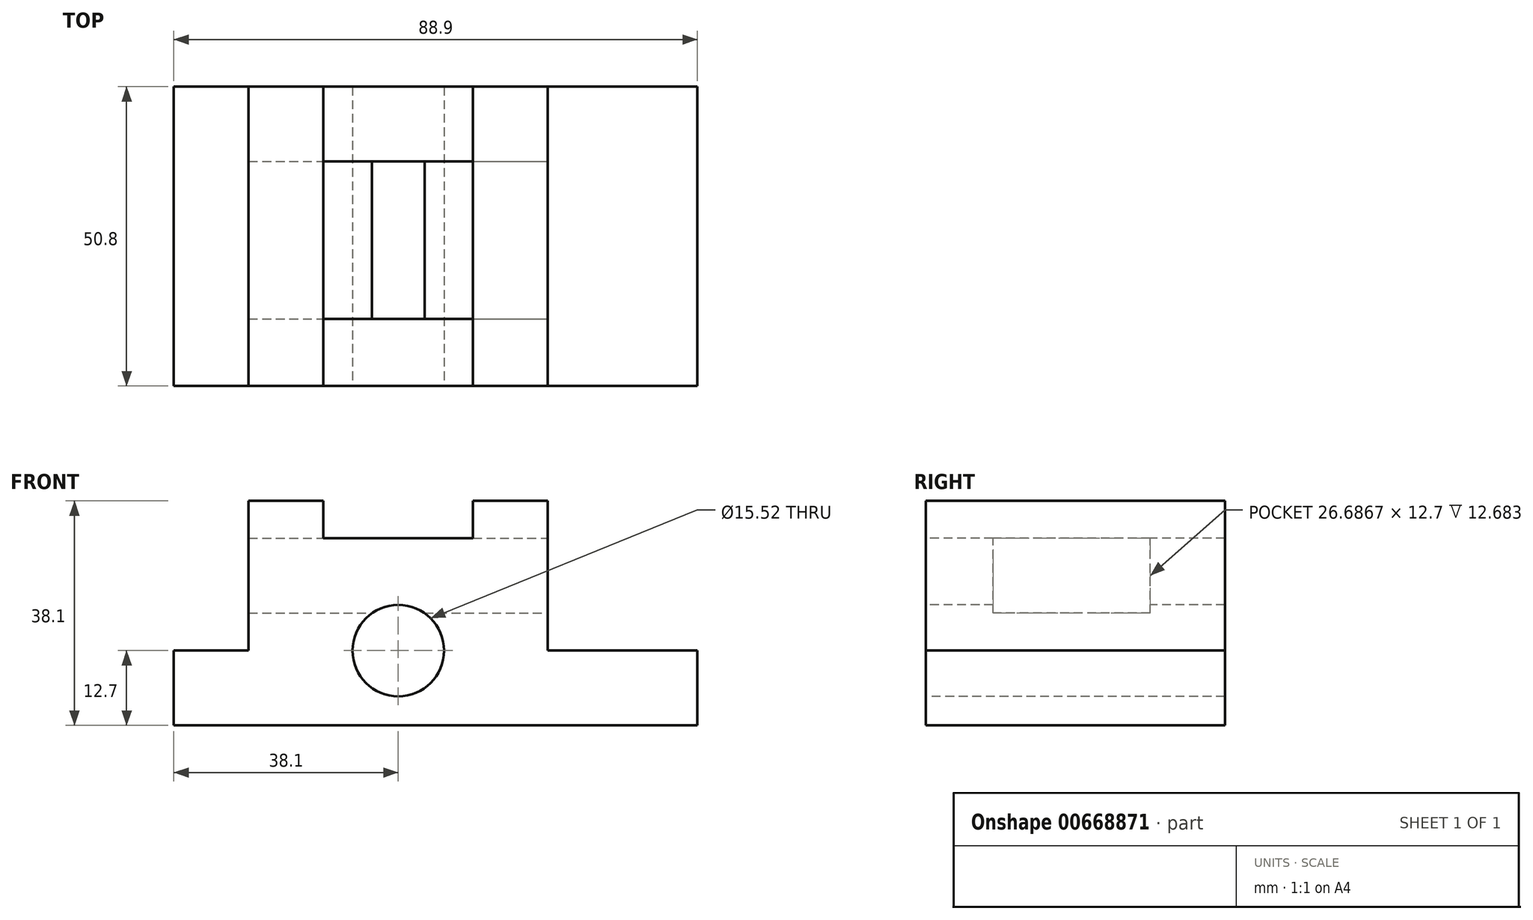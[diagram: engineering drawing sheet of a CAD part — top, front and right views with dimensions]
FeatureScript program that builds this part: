
annotation { "Feature Type Name" : "Feature", "Feature Type Description" : "" }
export const myFeature = defineFeature(function(context is Context, id is Id, definition is map)
    precondition{}
    {
        {
            var Q0;
            Q0=qCreatedBy(makeId("Front.planeOp"),FACE);
            var sketch = newSketch(context, id + "F0", { "sketchPlane" : qUnion([Q0])});
            skLineSegment(sketch, "E0.bottom", {"start": v(44.45, -19.05) * mm, "end": v(-44.45, -19.05) * mm});
            skLineSegment(sketch, "E0.top", {"start": v(44.45, 19.05) * mm, "end": v(-44.45, 19.05) * mm});
            skLineSegment(sketch, "E0.left", {"start": v(44.45, -19.05) * mm, "end": v(44.45, 19.05) * mm});
            skLineSegment(sketch, "E0.right", {"start": v(-44.45, -19.05) * mm, "end": v(-44.45, 19.05) * mm});
            skPoint(sketch, "E0.middle", {"position": v(0, 0) * mm});
            skSolve(sketch);
        }
        {
            var Q0;
            Q0=makeQuery(id+"F0.imprint","IMPRINT",FACE,{"disambiguationData":[TD([[makeQuery(id+"F0.imprint","IMPRINT",EDGE,{"derivedFrom":sQuery(id+"F0.wireOp",EDGE,"E0.bottom")}),-1.0]])]});
            extrude(context, id + "F1", {"entities" : qUnion([Q0]), "depth" : 50.8 * mm, "offsetDistance" : 25.4 * mm});
        }
        {
            var Q0;
            Q0=makeQuery(id+"F1.opExtrude","CAP_FACE",FACE,{"disambiguationData":[OSD([sQuery(id+"F0.wireOp",EDGE,"E0.bottom"),sQuery(id+"F0.wireOp",EDGE,"E0.top"),sQuery(id+"F0.wireOp",EDGE,"E0.left"),sQuery(id+"F0.wireOp",EDGE,"E0.right")])],"isStart":false});
            var sketch = newSketch(context, id + "F2", { "sketchPlane" : qUnion([Q0])});
            skLineSegment(sketch, "E1.bottom", {"start": v(44.45, 19.05) * mm, "end": v(19.05, 19.05) * mm});
            skLineSegment(sketch, "E1.top", {"start": v(44.45, -6.35) * mm, "end": v(19.05, -6.35) * mm});
            skLineSegment(sketch, "E1.left", {"start": v(44.45, 19.05) * mm, "end": v(44.45, -6.35) * mm});
            skLineSegment(sketch, "E1.right", {"start": v(19.05, 19.05) * mm, "end": v(19.05, -6.35) * mm});
            skSolve(sketch);
        }
        {
            var Q0;
            Q0 = qSketchRegion(id + "F2", true);
            extrude(context, id + "F3", {"entities" : qUnion([Q0]), "operationType" : NewBodyOperationType.REMOVE, "endBound" : BoundingType.THROUGH_ALL, "oppositeDirection" : true, "depth" : 25.4 * mm, "offsetDistance" : 25.4 * mm});
        }
        {
            var Q0;
            Q0=makeQuery(id+"F1.opExtrude","CAP_FACE",FACE,{"disambiguationData":[OSD([sQuery(id+"F0.wireOp",EDGE,"E0.bottom"),sQuery(id+"F0.wireOp",EDGE,"E0.top"),sQuery(id+"F0.wireOp",EDGE,"E0.left"),sQuery(id+"F0.wireOp",EDGE,"E0.right")])],"isStart":true});
            var sketch = newSketch(context, id + "F4", { "sketchPlane" : qUnion([Q0])});
            skLineSegment(sketch, "E2.bottom", {"start": v(44.45, 19.05) * mm, "end": v(31.75, 19.05) * mm});
            skLineSegment(sketch, "E2.top", {"start": v(44.45, -6.35) * mm, "end": v(31.75, -6.35) * mm});
            skLineSegment(sketch, "E2.left", {"start": v(44.45, 19.05) * mm, "end": v(44.45, -6.35) * mm});
            skLineSegment(sketch, "E2.right", {"start": v(31.75, 19.05) * mm, "end": v(31.75, -6.35) * mm});
            skSolve(sketch);
        }
        {
            var Q0;
            Q0 = qSketchRegion(id + "F4", true);
            extrude(context, id + "F5", {"entities" : qUnion([Q0]), "operationType" : NewBodyOperationType.REMOVE, "endBound" : BoundingType.THROUGH_ALL, "oppositeDirection" : true, "depth" : 25.4 * mm, "offsetDistance" : 25.4 * mm});
        }
        {
            var Q0;
            Q0=makeQuery(id+"F1.opExtrude","CAP_FACE",FACE,{"disambiguationData":[OSD([sQuery(id+"F0.wireOp",EDGE,"E0.bottom"),sQuery(id+"F0.wireOp",EDGE,"E0.top"),sQuery(id+"F0.wireOp",EDGE,"E0.left"),sQuery(id+"F0.wireOp",EDGE,"E0.right")])],"isStart":false});
            var sketch = newSketch(context, id + "F6", { "sketchPlane" : qUnion([Q0])});
            skLineSegment(sketch, "E3.bottom", {"start": v(6.35, 19.05) * mm, "end": v(-19.05, 19.05) * mm});
            skLineSegment(sketch, "E3.top", {"start": v(6.35, 12.7) * mm, "end": v(-19.05, 12.7) * mm});
            skLineSegment(sketch, "E3.left", {"start": v(6.35, 19.05) * mm, "end": v(6.35, 12.7) * mm});
            skLineSegment(sketch, "E3.right", {"start": v(-19.05, 19.05) * mm, "end": v(-19.05, 12.7) * mm});
            skSolve(sketch);
        }
        {
            var Q0;
            Q0=makeQuery(id+"F6.imprint","IMPRINT",FACE,{"disambiguationData":[TD([[makeQuery(id+"F6.imprint","IMPRINT",EDGE,{"derivedFrom":sQuery(id+"F6.wireOp",EDGE,"E3.bottom")}),1.0]])]});
            extrude(context, id + "F7", {"entities" : qUnion([Q0]), "operationType" : NewBodyOperationType.REMOVE, "endBound" : BoundingType.THROUGH_ALL, "oppositeDirection" : true, "depth" : 25.4 * mm, "offsetDistance" : 25.4 * mm});
        }
        {
            var Q0;
            Q0=makeQuery(id+"F1.opExtrude","CAP_FACE",FACE,{"disambiguationData":[OSD([sQuery(id+"F0.wireOp",EDGE,"E0.bottom"),sQuery(id+"F0.wireOp",EDGE,"E0.top"),sQuery(id+"F0.wireOp",EDGE,"E0.left"),sQuery(id+"F0.wireOp",EDGE,"E0.right")])],"isStart":false});
            var sketch = newSketch(context, id + "F8", { "sketchPlane" : qUnion([Q0])});
            skCircle(sketch, "E4", {"center": v(-6.35, -6.35) * mm, "radius": 7.76 * mm});
            skSolve(sketch);
        }
        {
            var Q0;
            Q0=makeQuery(id+"F7.boolean.opBoolean","COPY",FACE,{"derivedFrom":makeQuery(id+"F7.opExtrude","SWEPT_FACE",FACE,{"disambiguationData":[OSD([sQuery(id+"F6.wireOp",EDGE,"E3.top")])]})});
            var sketch = newSketch(context, id + "F9", { "sketchPlane" : qUnion([Q0])});
            skLineSegment(sketch, "E5.bottom", {"start": v(-31.73, -12.7) * mm, "end": v(19, -12.7) * mm});
            skLineSegment(sketch, "E5.top", {"start": v(-31.73, -39.39) * mm, "end": v(19, -39.39) * mm});
            skLineSegment(sketch, "E5.left", {"start": v(-31.73, -12.7) * mm, "end": v(-31.73, -39.39) * mm});
            skLineSegment(sketch, "E5.right", {"start": v(19, -12.7) * mm, "end": v(19, -39.39) * mm});
            skSolve(sketch);
        }
        {
            var Q0;
            Q0 = qSketchRegion(id + "F9", true);
            extrude(context, id + "F10", {"entities" : qUnion([Q0]), "operationType" : NewBodyOperationType.REMOVE, "oppositeDirection" : true, "depth" : 12.7 * mm, "offsetDistance" : 25.4 * mm});
        }
        {
            var Q0;
            Q0=makeQuery(id+"F8.imprint","IMPRINT",FACE,{"disambiguationData":[TD([[makeQuery(id+"F8.imprint","IMPRINT",EDGE,{"derivedFrom":sQuery(id+"F8.wireOp",EDGE,"E4")}),1.0]])]});
            extrude(context, id + "F11", {"entities" : qUnion([Q0]), "operationType" : NewBodyOperationType.REMOVE, "endBound" : BoundingType.THROUGH_ALL, "oppositeDirection" : true, "depth" : 25.4 * mm, "offsetDistance" : 25.4 * mm});
        }
    });
